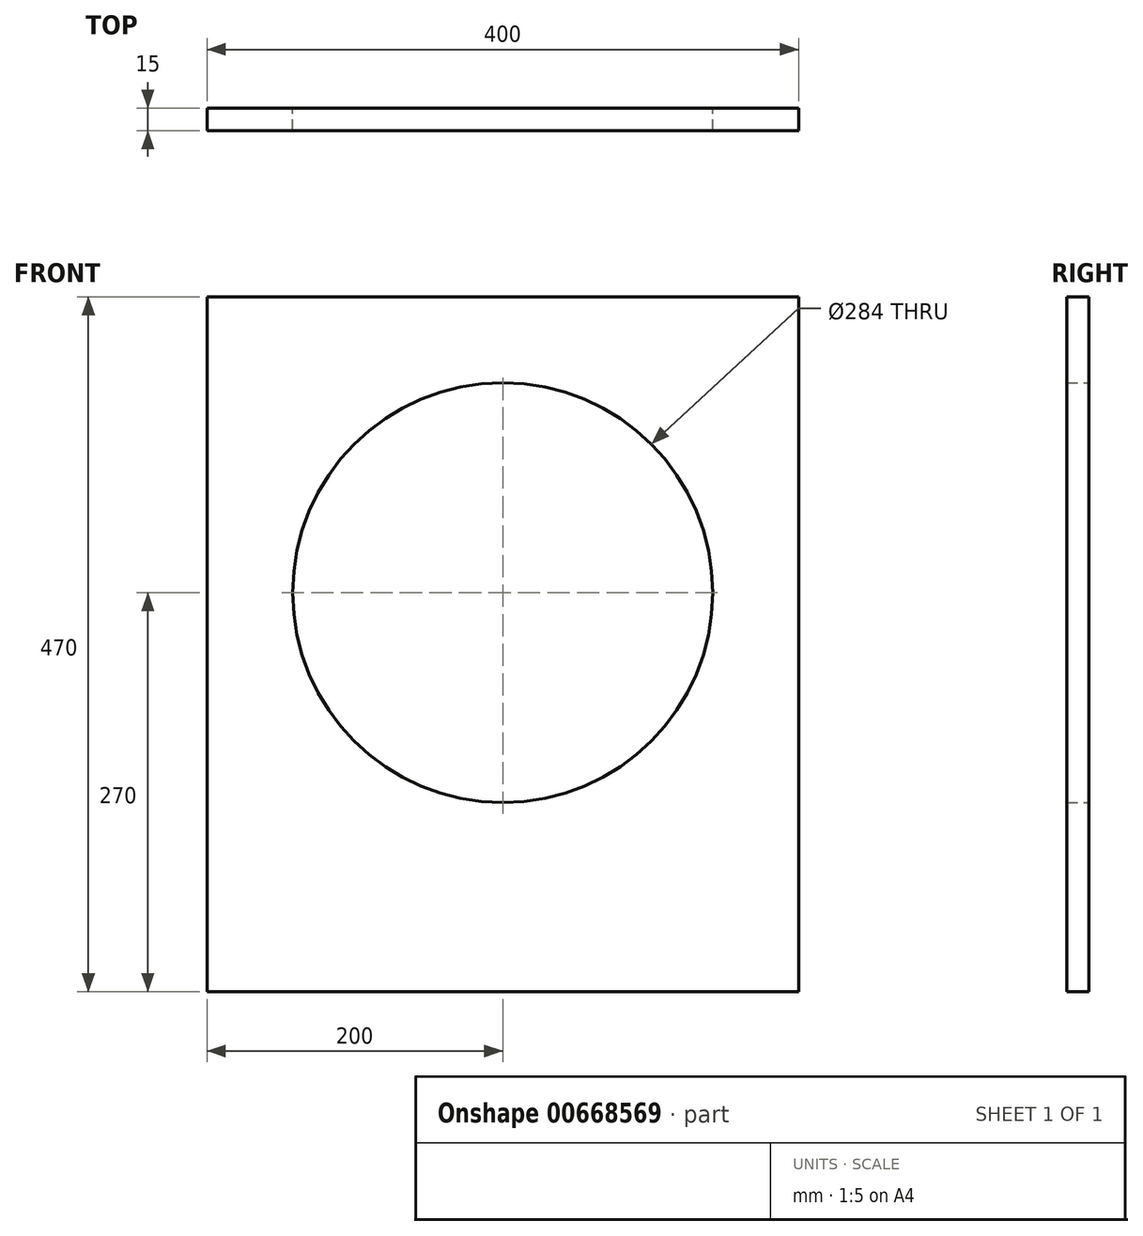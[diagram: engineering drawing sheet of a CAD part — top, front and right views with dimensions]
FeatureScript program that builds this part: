
annotation { "Feature Type Name" : "Feature", "Feature Type Description" : "" }
export const myFeature = defineFeature(function(context is Context, id is Id, definition is map)
    precondition{}
    {
        {
            var Q0;
            Q0=qCreatedBy(makeId("Front.planeOp"),FACE);
            var sketch = newSketch(context, id + "F0", { "sketchPlane" : qUnion([Q0])});
            skLineSegment(sketch, "E0.bottom", {"start": v(0, 0) * mm, "end": v(400, 0) * mm});
            skLineSegment(sketch, "E0.top", {"start": v(0, 470) * mm, "end": v(400, 470) * mm});
            skLineSegment(sketch, "E0.left", {"start": v(0, 0) * mm, "end": v(0, 470) * mm});
            skLineSegment(sketch, "E0.right", {"start": v(400, 0) * mm, "end": v(400, 470) * mm});
            skCircle(sketch, "E1", {"center": v(200, 270) * mm, "radius": 142 * mm});
            skSolve(sketch);
        }
        {
            var Q0;
            Q0=makeQuery(id+"F0.imprint","IMPRINT",FACE,{"disambiguationData":[TD([[makeQuery(id+"F0.imprint","IMPRINT",EDGE,{"derivedFrom":sQuery(id+"F0.wireOp",EDGE,"E0.bottom")}),1.0]])]});
            extrude(context, id + "F1", {"entities" : qUnion([Q0]), "depth" : 15 * mm, "offsetDistance" : 25 * mm});
        }
    });
